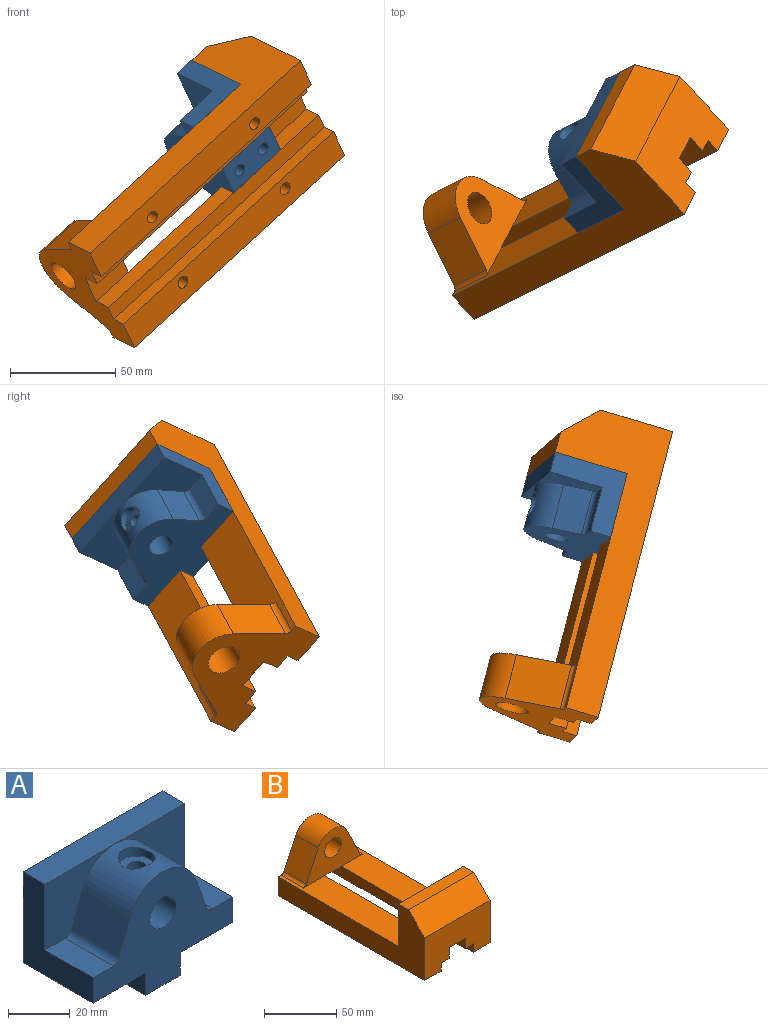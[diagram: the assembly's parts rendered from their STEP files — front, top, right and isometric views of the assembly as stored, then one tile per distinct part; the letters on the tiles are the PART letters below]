
ASSEMBLY  parts=2 mates=1
PART A: 28 faces, bbox 64x32x45 mm
  f0: cylinder r=16mm len=30.07mm, axis (0,1,0), area 745.1mm2, adj f7,f8,f13,f14,f17,f21
  f1: cylinder r=6mm len=22mm, axis (0,1,0), area 800.1mm2, adj f13,f18,f22
  f2: plane 32x16mm, normal (0,0,-1), area 455.5mm2, adj f3,f12,f13,f15,f25,f27
  f3: plane 32x9mm, normal (1,0,0), area 288mm2, adj f2,f4,f13,f15
  f4: plane 32x24mm, normal (0,0,-1), area 768mm2, adj f3,f5,f13,f15
  f5: plane 36x32mm, normal (1,0,0), area 580mm2, adj f4,f6,f13,f14,f15,f16
  f6: plane 22x9.24mm, normal (0,0,1), area 203.2mm2, adj f5,f13,f14,f20
  f7: plane 22x13.5mm, normal (0.94,0,0.34), area 315.9mm2, adj f0,f13,f14,f20
  f8: plane 22x13.5mm, normal (-0.94,0,0.34), area 315.9mm2, adj f0,f13,f17,f19
  f9: plane 22x9.24mm, normal (0,0,1), area 203.2mm2, adj f10,f13,f17,f19
  f10: plane 36x32mm, normal (-1,0,0), area 580mm2, adj f9,f11,f13,f15,f16,f17
  f11: plane 32x24mm, normal (0,0,-1), area 768mm2, adj f10,f12,f13,f15
  f12: plane 32x9mm, normal (-1,0,0), area 288mm2, adj f2,f11,f13,f15
  f13: plane 64x45mm, normal (0,-1,0), area 1455.3mm2, adj f0,f1,f2,f3,f4,f5,f6,f7
  f14: plane 32x26mm, normal (0,-1,0), area 439.8mm2, adj f0,f5,f6,f7,f16,f20
  f15: plane 64x45mm, normal (0,1,0), area 2448mm2, adj f2,f3,f4,f5,f10,f11,f12,f16
  f16: plane 64x10mm, normal (0,0,1), area 640mm2, adj f5,f10,f14,f15,f17
  f17: plane 32x26mm, normal (0,-1,0), area 439.8mm2, adj f0,f8,f9,f10,f16,f19
  f18: plane 12x12mm, normal (0,-1,0), area 113.1mm2, adj f1
  f19: cylinder r=3mm len=22mm, axis (0,1,0), area 80.6mm2, adj f8,f9,f13,f17
  f20: cylinder r=3mm len=22mm, axis (0,-1,0), area 80.6mm2, adj f6,f7,f13,f14
  f21: cylinder r=6mm len=12mm, axis (0,0,1), area 129mm2, adj f0,f23
  f22: cylinder r=3mm len=6.8mm, axis (0,0,1), area 120.5mm2, adj f1,f23
  f23: plane 12x12mm, normal (0,0,1), area 84.8mm2, adj f21,f22
  f24: cone r=0mm half-angle=59deg, axis (0,0,-1), area 33mm2, adj f25
  f25: cylinder r=3mm len=16mm, axis (0,0,-1), area 301.6mm2, adj f2,f24
  f26: cone r=0mm half-angle=59deg, axis (0,0,-1), area 33mm2, adj f27
  f27: cylinder r=3mm len=16mm, axis (0,0,-1), area 301.6mm2, adj f2,f26
PART B: 34 faces, bbox 64x144x52 mm
  f0: plane 144x16mm, normal (0,0,-1), area 2247.5mm2, adj f2,f5,f10,f18,f29,f31
  f1: plane 118x24mm, normal (0,0,1), area 2372.4mm2, adj f5,f6,f9,f15,f22,f32
  f2: plane 64x36mm, normal (0,-1,0), area 1936.2mm2, adj f0,f4,f8,f9,f10,f17,f18,f19
  f3: plane 118x24mm, normal (0,0,1), area 2372.4mm2, adj f5,f6,f10,f15,f20,f33
  f4: plane 144x16mm, normal (0,0,-1), area 2247.5mm2, adj f2,f5,f9,f17,f25,f27
  f5: plane 64x52mm, normal (0,1,0), area 1758.8mm2, adj f0,f1,f3,f4,f9,f10,f11,f12
  f6: plane 64x36mm, normal (0,1,0), area 2304mm2, adj f1,f3,f7,f9,f10,f21
  f7: plane 64x10mm, normal (0,0,1), area 640mm2, adj f6,f8,f9,f10
  f8: plane 64x16mm, normal (0,-0.71,0.71), area 1448.2mm2, adj f2,f7,f9,f10
  f9: plane 144x52mm, normal (1,0,0), area 3112mm2, adj f1,f2,f4,f5,f6,f7,f8
  f10: plane 144x52mm, normal (-1,0,0), area 3112mm2, adj f0,f2,f3,f5,f6,f7,f8
  f11: cylinder r=16mm len=29mm, axis (0,1,0), area 798.7mm2, adj f5,f12,f14,f15
  f12: plane 25.03x22mm, normal (0.91,0,0.42), area 607.6mm2, adj f5,f11,f15,f32
  f13: cylinder r=8mm len=22mm, axis (0,1,0), area 1105.8mm2, adj f5,f15
  f14: plane 25.03x22mm, normal (-0.91,0,0.42), area 607.6mm2, adj f5,f11,f15,f33
  f15: plane 57.78x36mm, normal (0,-1,0), area 1102.7mm2, adj f1,f3,f11,f12,f13,f14,f16,f32
  f16: plane 22x16mm, normal (0,0,-1), area 352mm2, adj f5,f15,f20,f22
  f17: plane 144x7mm, normal (-1,0,0), area 1008mm2, adj f2,f4,f5,f23
  f18: plane 144x6.98mm, normal (1,0,0), area 1005.2mm2, adj f0,f2,f5,f19
  f19: plane 144x8mm, normal (0,0,-1), area 1152mm2, adj f2,f5,f18,f20
  f20: plane 144x9.02mm, normal (1,0,0), area 1298.8mm2, adj f2,f3,f5,f16,f19,f21
  f21: plane 26x16mm, normal (0,0,-1), area 416mm2, adj f2,f6,f20,f22
  f22: plane 144x9mm, normal (-1,0,0), area 1296mm2, adj f1,f2,f5,f16,f21,f23
  f23: plane 144x8mm, normal (0,0,-1), area 1152mm2, adj f2,f5,f17,f22
  f24: cone r=0mm half-angle=59deg, axis (0,0,-1), area 33mm2, adj f25
  f25: cylinder r=3mm len=10mm, axis (0,0,-1), area 188.5mm2, adj f4,f24
  f26: cone r=0mm half-angle=59deg, axis (0,0,-1), area 33mm2, adj f27
  f27: cylinder r=3mm len=10mm, axis (0,0,-1), area 188.5mm2, adj f4,f26
  f28: cone r=0mm half-angle=59deg, axis (0,0,-1), area 33mm2, adj f29
  f29: cylinder r=3mm len=10mm, axis (0,0,-1), area 188.5mm2, adj f0,f28
  f30: cone r=0mm half-angle=59deg, axis (0,0,-1), area 33mm2, adj f31
  f31: cylinder r=3mm len=10mm, axis (0,0,-1), area 188.5mm2, adj f0,f30
  f32: cylinder r=3mm len=22mm, axis (0,-1,0), area 74.9mm2, adj f1,f5,f12,f15
  f33: cylinder r=3mm len=22mm, axis (0,1,0), area 74.9mm2, adj f3,f5,f14,f15
PLACE A rot(axis=(-0.03,-0.71,-0.7),109.4deg) t=(-11.68,91.54,-129.07)mm
PLACE B rot(axis=(-0.71,0.03,0.7),110.3deg) t=(-31.72,74.42,-153.78)mm
MATE slider A.f15 <-> B.f6  axis (0.69,0.35,0.63) through (0.02,121.4,-142.35)mm
